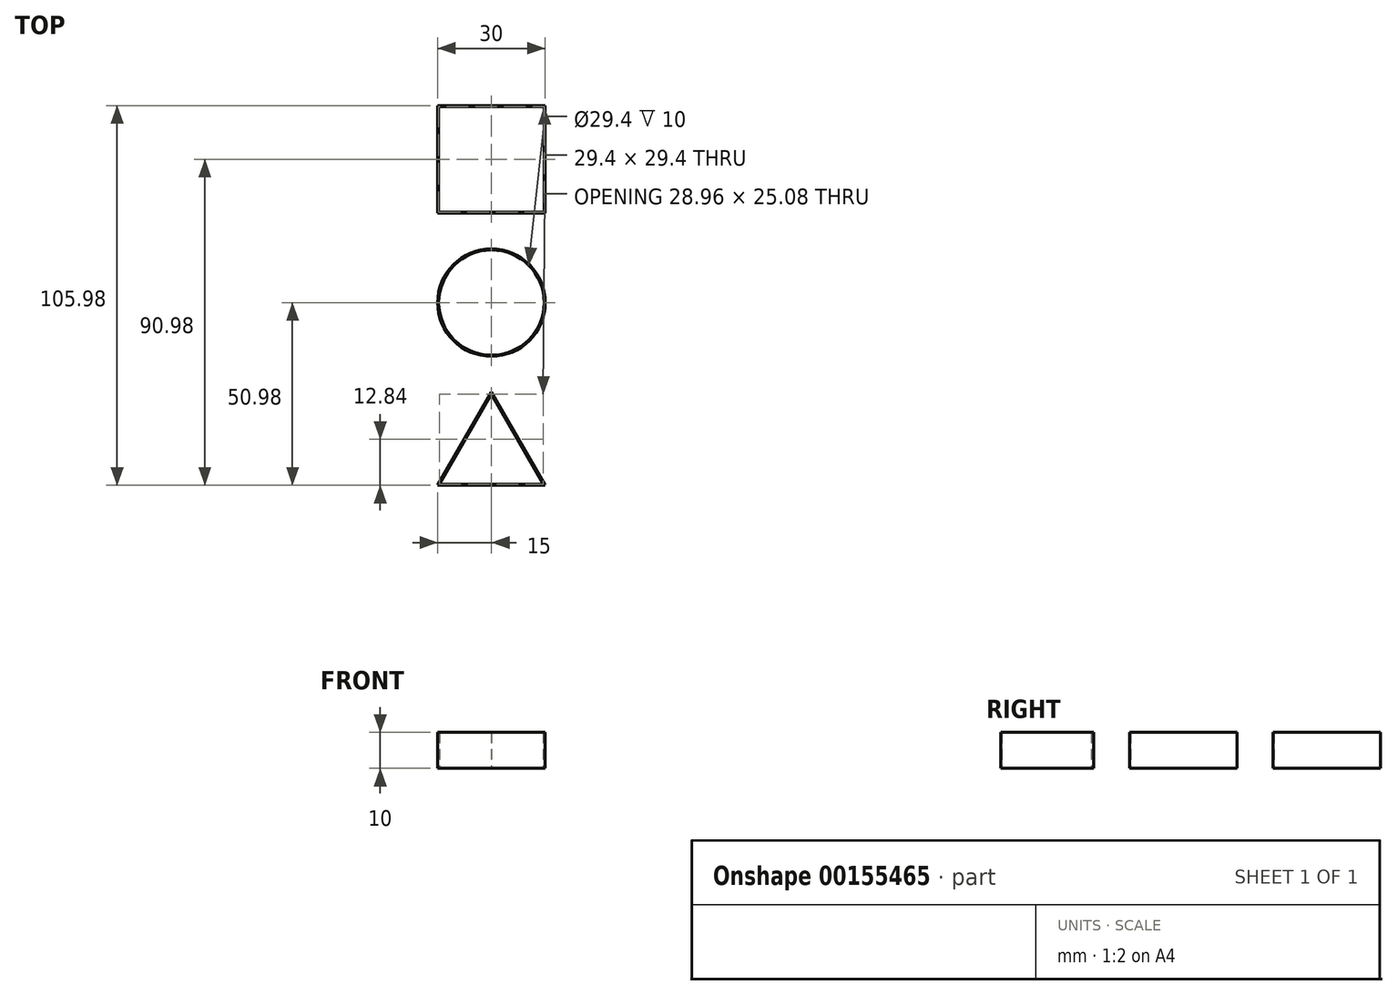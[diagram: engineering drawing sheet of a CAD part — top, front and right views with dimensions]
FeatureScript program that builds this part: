
annotation { "Feature Type Name" : "Feature", "Feature Type Description" : "" }
export const myFeature = defineFeature(function(context is Context, id is Id, definition is map)
    precondition{}
    {
        {
            var Q0;
            Q0=qCreatedBy(makeId("Top.planeOp"),FACE);
            var sketch = newSketch(context, id + "F0", { "sketchPlane" : qUnion([Q0])});
            skCircle(sketch, "E0", {"center": v(0, 0) * mm, "radius": 15 * mm});
            skCircle(sketch, "E1", {"center": v(0, 0) * mm, "radius": 14.7 * mm});
            skLineSegment(sketch, "E2.bottom", {"start": v(15, 55) * mm, "end": v(-15, 55) * mm});
            skLineSegment(sketch, "E2.top", {"start": v(15, 25) * mm, "end": v(-15, 25) * mm});
            skLineSegment(sketch, "E2.left", {"start": v(15, 55) * mm, "end": v(15, 25) * mm});
            skLineSegment(sketch, "E2.right", {"start": v(-15, 55) * mm, "end": v(-15, 25) * mm});
            skPoint(sketch, "E2.middle", {"position": v(0, 40) * mm});
            skLineSegment(sketch, "E3.bottom", {"start": v(14.7, 54.7) * mm, "end": v(-14.7, 54.7) * mm});
            skLineSegment(sketch, "E3.top", {"start": v(14.7, 25.3) * mm, "end": v(-14.7, 25.3) * mm});
            skLineSegment(sketch, "E3.left", {"start": v(14.7, 54.7) * mm, "end": v(14.7, 25.3) * mm});
            skLineSegment(sketch, "E3.right", {"start": v(-14.7, 54.7) * mm, "end": v(-14.7, 25.3) * mm});
            skLineSegment(sketch, "E4", {"start": v(0, -25) * mm, "end": v(-15, -50.98) * mm});
            skLineSegment(sketch, "E5", {"start": v(-15, -50.98) * mm, "end": v(15, -50.98) * mm});
            skLineSegment(sketch, "E6", {"start": v(15, -50.98) * mm, "end": v(0, -25) * mm});
            skLineSegment(sketch, "E7.0", {"start": v(0, -25.6) * mm, "end": v(-14.48, -50.68) * mm});
            skLineSegment(sketch, "E7.1", {"start": v(14.48, -50.68) * mm, "end": v(0, -25.6) * mm});
            skLineSegment(sketch, "E7.2", {"start": v(-14.48, -50.68) * mm, "end": v(14.48, -50.68) * mm});
            skSolve(sketch);
        }
        {
            var Q0;
            Q0 = qSketchRegion(id + "F0", true);
            extrude(context, id + "F1", {"entities" : qUnion([Q0]), "depth" : 10 * mm});
        }
    });
